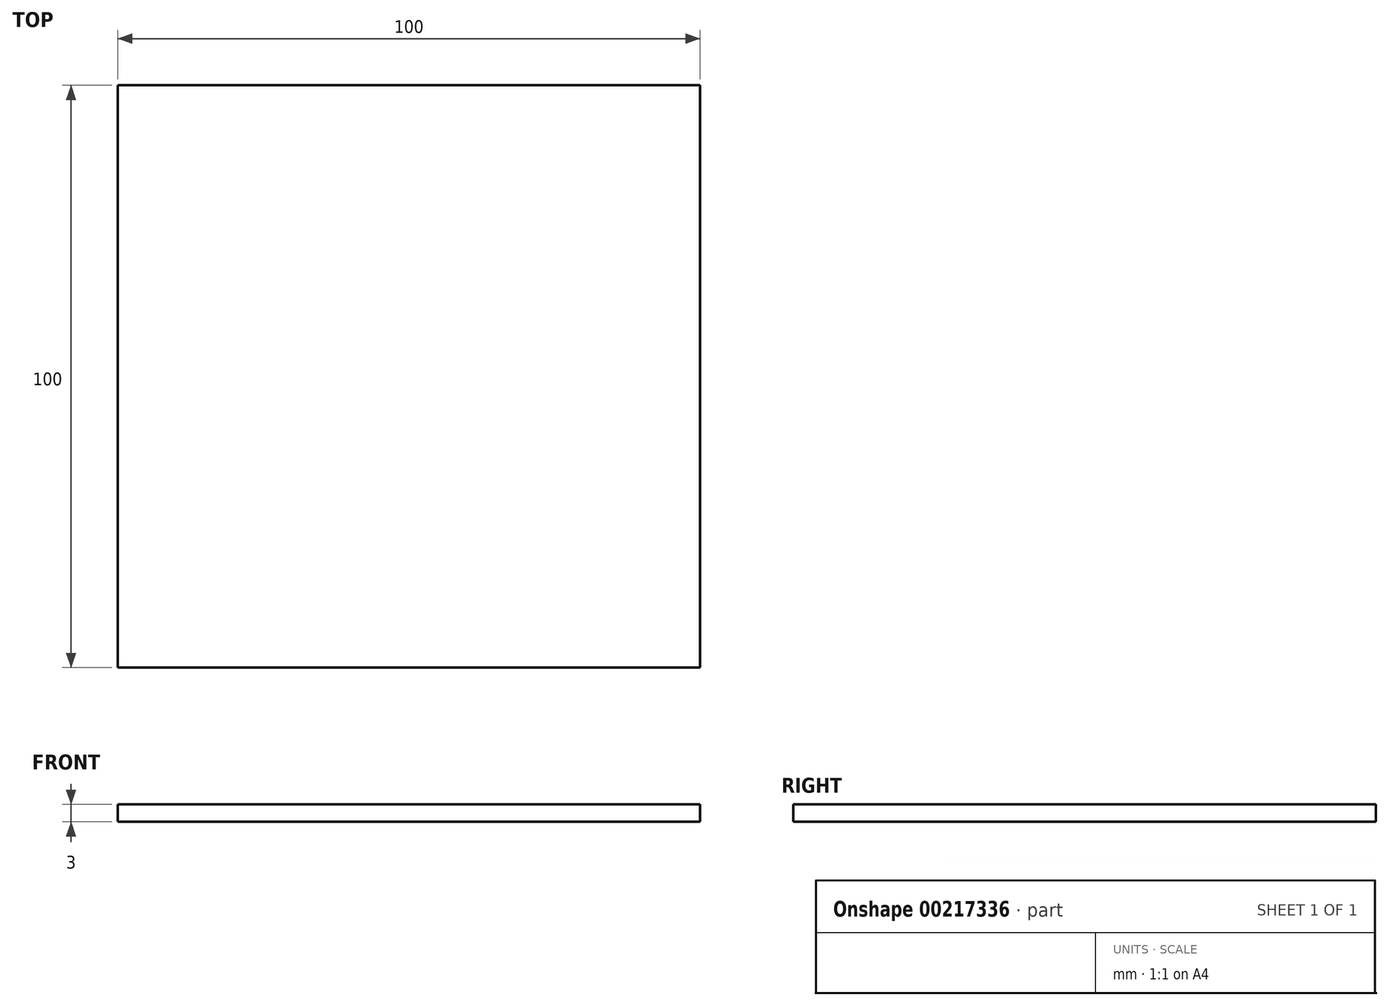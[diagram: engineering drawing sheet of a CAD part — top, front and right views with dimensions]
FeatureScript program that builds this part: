
annotation { "Feature Type Name" : "Feature", "Feature Type Description" : "" }
export const myFeature = defineFeature(function(context is Context, id is Id, definition is map)
    precondition{}
    {
        {
            var Q0;
            Q0=qCreatedBy(makeId("Top.planeOp"),FACE);
            var sketch = newSketch(context, id + "F0", { "sketchPlane" : qUnion([Q0])});
            skLineSegment(sketch, "E0.bottom", {"start": v(50, 50) * mm, "end": v(-50, 50) * mm});
            skLineSegment(sketch, "E0.top", {"start": v(50, -50) * mm, "end": v(-50, -50) * mm});
            skLineSegment(sketch, "E0.left", {"start": v(50, 50) * mm, "end": v(50, -50) * mm});
            skLineSegment(sketch, "E0.right", {"start": v(-50, 50) * mm, "end": v(-50, -50) * mm});
            skPoint(sketch, "E0.middle", {"position": v(0, 0) * mm});
            skSolve(sketch);
        }
        {
            var Q0;
            Q0=makeQuery(id+"F0.imprint","IMPRINT",FACE,{"disambiguationData":[TD([[makeQuery(id+"F0.imprint","IMPRINT",EDGE,{"derivedFrom":sQuery(id+"F0.wireOp",EDGE,"E0.bottom")}),1.0]])]});
            extrude(context, id + "F1", {"entities" : qUnion([Q0]), "depth" : 3 * mm});
        }
    });
